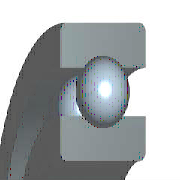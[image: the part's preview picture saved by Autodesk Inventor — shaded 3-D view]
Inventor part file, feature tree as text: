
AUTODESK INVENTOR PART (.ipt)
format: ipt  version: 2021 (Build 250183000, 183)  size: 472,064 bytes
history: native  units: mm (DEFAULTED — no unit token found)
features: sketch x5, other x3, plane x2, pattern_circular x1, fillet x1
ambient origin geometry x8: Origin, YZ Plane, XZ Plane, XY Plane, X Axis, Y Axis, Z Axis, Center Point
bodies: Solid1 (feature_tree)
feature tree (12):
  sketch  "Sketch1"  dims[d2=72.0mm]
  other  "WorkPoint1"
  other  "WorkAxis1"
  plane  "WorkPlane3"
  plane  "WorkPlane4"
  sketch  "Sketch4"  dims[d5=7.0mm]
  other  "WorkPoint2"
  pattern_circular  "PolarArray1"  Count=2  [1 undecoded]
  fillet  "Fillet1"  Radius=30.0mm
  sketch  "Sketch2"  dims[d3=42.0mm]
  sketch  "Sketch3"  dims[d4=19.0mm]
  sketch  "Sketch5"  dims[d6=360.0deg d7=0.0mm d8=15.6mm d9=3.6mm d10=360.0deg d11=-7.0mm d12=0.0mm d13=0.0mm d14=15.6001mm d15=3.6001mm d16=360.0deg d17=154.0mm d19=360.0deg d20=0.3mm d21=16.92mm d22=18.0mm d23=19.08mm d26=0.0mm d27=0.0mm d28=0.0mm d29=0.0mm d30=0.0mm]
note: 1 required parameter value undecoded (feature->parameter linkage not recoverable at this tier; creation-order binding heuristic only, values carry confidence <= 0.55)
